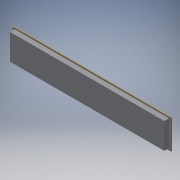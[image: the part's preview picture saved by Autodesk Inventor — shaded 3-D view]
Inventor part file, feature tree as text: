
AUTODESK INVENTOR PART (.ipt)
format: ipt  version: 2019 (Build 230136000, 136)  size: 102,400 bytes
history: native  units: mm
features: other x6, reference x4, extrude x2, sketch x2
ambient origin geometry x8: Origin, YZ Plane, XZ Plane, XY Plane, X Axis, Y Axis, Z Axis, Center Point
bodies: Solid1 (feature_tree)
feature tree (14):
  extrude  "Extrusion1"  Depth=861.06mm
  extrude  "Extrusion2"  Depth=25.4mm TaperAngle=0.0deg
  sketch  "Sketch1"  dims[d0=4.7625mm d1=0.0mm d2=861.06mm]
  sketch  "Sketch2"  dims[d3=160.02mm d4=25.4mm d5=0.0mm]
  reference  "Reference1"
  reference  "Reference2"
  reference  "Reference3"
  reference  "Reference4"
  parser-record x1  (decoder bookkeeping rows leaked as tree rows — omitted from the tree; the rows remain in map.json)
  other  "enclosure.iam"
  other  "1515-S-BLACK_breadboard_base:2"
  other  "1530-S-BLACK_base_side:2"
  other  "1530-S-BLACK_base_front:1"
  other  "1530-S-BLACK_base_front:2"
note: 1 file-system path scrubbed to <path> (originals preserved in map.json)
